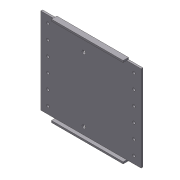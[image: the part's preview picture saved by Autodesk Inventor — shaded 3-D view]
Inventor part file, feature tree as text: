
AUTODESK INVENTOR PART (.ipt)
format: ipt  version: 2012 (Build 160160000, 160)  size: 138,240 bytes
history: native  units: in
note: dims shown in document units (in); Inventor stores cm internally (conversion verified against a paired STEP export)
features: extrude x4, sketch x4
ambient origin geometry x8: Origin, YZ Plane, XZ Plane, XY Plane, X Axis, Y Axis, Z Axis, Center Point
feature tree (8):
  extrude  "Extrusion3"  Depth=7.0in
  extrude  "Extrusion4"  Depth=1.0in
  extrude  "Extrusion5"  Depth=0.125in TaperAngle=0.0deg
  extrude  "Extrusion7"  Depth=1.0in
  sketch  "Sketch1"  dims[d0=6.0in d1=7.0in]
  sketch  "Sketch2"  dims[d18=1.0in d19=1.0in]
  sketch  "Sketch3"  dims[d20=0.125in d24=0.125in d25=0.0in]
  sketch  "Sketch5"  dims[d26=0.5in d27=1.0in d28=0.1875in d29=0.5in d30=1.0in d31=0.1875in d32=0.125in d33=0.0in d34=3.0in d35=3.0in d36=4.5in d37=0.5in d38=0.25in d39=0.25in d40=0.125in d41=0.0in d49=0.25in d50=0.0in]
